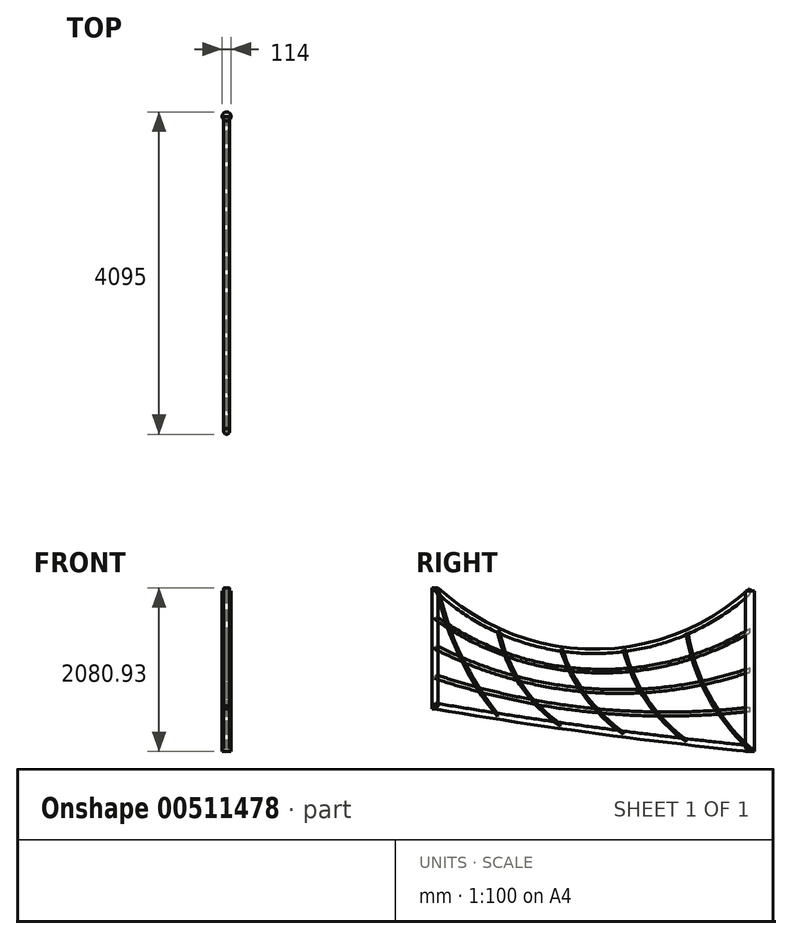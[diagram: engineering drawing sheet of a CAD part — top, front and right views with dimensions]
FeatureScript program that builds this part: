
annotation { "Feature Type Name" : "Feature", "Feature Type Description" : "" }
export const myFeature = defineFeature(function(context is Context, id is Id, definition is map)
    precondition{}
    {
        {
            var Q0;
            Q0=qCreatedBy(makeId("Right.planeOp"),FACE);
            var sketch = newSketch(context, id + "F0", { "sketchPlane" : qUnion([Q0])});
            skLineSegment(sketch, "E0.top", {"start": v(0, 2000) * mm, "end": v(-4000, 2000) * mm});
            skLineSegment(sketch, "E0.left", {"start": v(0, 0) * mm, "end": v(0, 2000) * mm});
            skLineSegment(sketch, "E0.right", {"start": v(-4000, 0) * mm, "end": v(-4000, 2000) * mm});
            skPoint(sketch, "E1", {"position": v(-4000, 540) * mm});
            skPoint(sketch, "E2", {"position": v(-4000, 915) * mm});
            skPoint(sketch, "E3", {"position": v(-4000, 1290) * mm});
            skPoint(sketch, "E4", {"position": v(-4000, 2040) * mm});
            skPoint(sketch, "E5", {"position": v(0, 500) * mm});
            skPoint(sketch, "E6", {"position": v(0, 1000) * mm});
            skPoint(sketch, "E7", {"position": v(0, 1500) * mm});
            skPoint(sketch, "E8", {"position": v(-4000, 1665) * mm});
            skPoint(sketch, "E9", {"position": v(-2000, 0) * mm});
            skPoint(sketch, "E10", {"position": v(-2000, 486.4) * mm});
            skPoint(sketch, "E11", {"position": v(-2000, 736.4) * mm});
            skPoint(sketch, "E12", {"position": v(-2000, 1236.4) * mm});
            skPoint(sketch, "E13", {"position": v(-2000, 986.4) * mm});
            skArc(sketch, "E14", {"start": v(-4000, 540) * mm, "mid": v(-2004.45, 237) * mm, "end": v(0, 0) * mm});
            skPoint(sketch, "E15", {"position": v(-2000, 236.4) * mm});
            skArc(sketch, "E16", {"start": v(-4000, 915) * mm, "mid": v(-2022.7, 488.74) * mm, "end": v(0, 500) * mm});
            skArc(sketch, "E17", {"start": v(-4000, 1290) * mm, "mid": v(-2029.47, 738.46) * mm, "end": v(0, 1000) * mm});
            skArc(sketch, "E18", {"start": v(-4000, 1665) * mm, "mid": v(-2024.55, 987.34) * mm, "end": v(0, 1500) * mm});
            skArc(sketch, "E19", {"start": v(-4000, 2040) * mm, "mid": v(-2007.84, 1236.48) * mm, "end": v(0, 2000) * mm});
            skSolve(sketch);
        }
        {
            var Q0;
            Q0=qCreatedBy(makeId("Front.planeOp"),FACE);
            var sketch = newSketch(context, id + "F1", { "sketchPlane" : qUnion([Q0])});
            skCircle(sketch, "E20", {"center": v(0, 0) * mm, "radius": 38 * mm});
            skCircle(sketch, "E21", {"center": v(0, 500) * mm, "radius": 25.5 * mm});
            skCircle(sketch, "E22", {"center": v(0, 1000) * mm, "radius": 25.5 * mm});
            skCircle(sketch, "E23", {"center": v(0, 1500) * mm, "radius": 25.5 * mm});
            skCircle(sketch, "E24", {"center": v(0, 2000) * mm, "radius": 38 * mm});
            skSolve(sketch);
        }
        {
            var Q0;
            Q0=makeQuery(id+"F1.imprint","IMPRINT",FACE,{"disambiguationData":[TD([[makeQuery(id+"F1.imprint","IMPRINT",EDGE,{"derivedFrom":sQuery(id+"F1.wireOp",EDGE,"E20")}),1.0]])]});
            var Q1;
            Q1=sQuery(id+"F0.wireOp",EDGE,"E14");
            sweep(context, id + "F2", {"profiles" : qUnion([Q0]), "path" : qUnion([Q1])});
        }
        {
            var Q0;
            Q0=makeQuery(id+"F1.imprint","IMPRINT",FACE,{"disambiguationData":[TD([[makeQuery(id+"F1.imprint","IMPRINT",EDGE,{"derivedFrom":sQuery(id+"F1.wireOp",EDGE,"E21")}),1.0]])]});
            var Q1;
            Q1=sQuery(id+"F0.wireOp",EDGE,"E16");
            sweep(context, id + "F3", {"profiles" : qUnion([Q0]), "path" : qUnion([Q1])});
        }
        {
            var Q0;
            Q0=makeQuery(id+"F1.imprint","IMPRINT",FACE,{"disambiguationData":[TD([[makeQuery(id+"F1.imprint","IMPRINT",EDGE,{"derivedFrom":sQuery(id+"F1.wireOp",EDGE,"E22")}),1.0]])]});
            var Q1;
            Q1=sQuery(id+"F0.wireOp",EDGE,"E17");
            sweep(context, id + "F4", {"profiles" : qUnion([Q0]), "path" : qUnion([Q1])});
        }
        {
            var Q0;
            Q0=makeQuery(id+"F1.imprint","IMPRINT",FACE,{"disambiguationData":[TD([[makeQuery(id+"F1.imprint","IMPRINT",EDGE,{"derivedFrom":sQuery(id+"F1.wireOp",EDGE,"E23")}),1.0]])]});
            var Q1;
            Q1=sQuery(id+"F0.wireOp",EDGE,"E18");
            sweep(context, id + "F5", {"profiles" : qUnion([Q0]), "path" : qUnion([Q1])});
        }
        {
            var Q0;
            Q0=makeQuery(id+"F1.imprint","IMPRINT",FACE,{"disambiguationData":[TD([[makeQuery(id+"F1.imprint","IMPRINT",EDGE,{"derivedFrom":sQuery(id+"F1.wireOp",EDGE,"E24")}),1.0]])]});
            var Q1;
            Q1=sQuery(id+"F0.wireOp",EDGE,"E19");
            sweep(context, id + "F6", {"profiles" : qUnion([Q0]), "path" : qUnion([Q1])});
        }
        {
            var Q0;
            Q0=qCreatedBy(makeId("Top.planeOp"),FACE);
            var sketch = newSketch(context, id + "F7", { "sketchPlane" : qUnion([Q0])});
            skCircle(sketch, "E25", {"center": v(0, 0) * mm, "radius": 57 * mm});
            skSolve(sketch);
        }
        {
            var Q0;
            Q0=makeQuery(id+"F7.imprint","IMPRINT",FACE,{"disambiguationData":[TD([[makeQuery(id+"F7.imprint","IMPRINT",EDGE,{"derivedFrom":sQuery(id+"F7.wireOp",EDGE,"E25")}),1.0]])]});
            extrude(context, id + "F8", {"entities" : qUnion([Q0]), "depth" : 2000 * mm});
        }
        {
            var Q0;
            Q0=qCreatedBy(makeId("Top.planeOp"),FACE);
            cPlane(context, id + "F9", {"entities" : qUnion([Q0]), "cplaneType" : CPlaneType.OFFSET, "offset" : 540 * mm, "width" : 150 * mm, "height" : 150 * mm});
        }
        {
            var Q0;
            Q0=qCreatedBy(id+"F9.planeOp",FACE);
            var sketch = newSketch(context, id + "F10", { "sketchPlane" : qUnion([Q0])});
            skPoint(sketch, "E26", {"position": v(0, 0) * mm});
            skCircle(sketch, "E27", {"center": v(0, -4000) * mm, "radius": 38 * mm});
            skSolve(sketch);
        }
        {
            var Q0;
            Q0=makeQuery(id+"F10.imprint","IMPRINT",FACE,{"disambiguationData":[TD([[makeQuery(id+"F10.imprint","IMPRINT",EDGE,{"derivedFrom":sQuery(id+"F10.wireOp",EDGE,"E27")}),1.0]])]});
            extrude(context, id + "F11", {"entities" : qUnion([Q0]), "depth" : 1500 * mm});
        }
        {
            var Q0;
            Q0=makeQuery(id+"F11.opExtrude","CAP_FACE",FACE,{"disambiguationData":[OSD([sQuery(id+"F10.wireOp",EDGE,"E27")])],"isStart":true});
            extrude(context, id + "F12", {"entities" : qUnion([Q0]), "depth" : 38 * mm});
        }
        {
            var Q0;
            Q0=makeQuery(id+"F8.opExtrude","CAP_FACE",FACE,{"disambiguationData":[OSD([sQuery(id+"F7.wireOp",EDGE,"E25")])],"isStart":true});
            extrude(context, id + "F13", {"entities" : qUnion([Q0]), "depth" : 38 * mm});
        }
        {
            var Q0;
            Q0=qCreatedBy(makeId("Right.planeOp"),FACE);
            var sketch = newSketch(context, id + "F14", { "sketchPlane" : qUnion([Q0])});
            skLineSegment(sketch, "E28.bottom", {"start": v(0, 0) * mm, "end": v(-4000, 0) * mm});
            skLineSegment(sketch, "E28.top", {"start": v(0, 2000) * mm, "end": v(-4000, 2000) * mm});
            skLineSegment(sketch, "E28.left", {"start": v(0, 0) * mm, "end": v(0, 2000) * mm});
            skLineSegment(sketch, "E28.right", {"start": v(-4000, 0) * mm, "end": v(-4000, 2000) * mm});
            skPoint(sketch, "E29", {"position": v(-800, 0) * mm});
            skPoint(sketch, "E30", {"position": v(-1600, 0) * mm});
            skPoint(sketch, "E31", {"position": v(-2400, 0) * mm});
            skPoint(sketch, "E32", {"position": v(-3200, 0) * mm});
            skArc(sketch, "E33", {"start": v(-800, 1473.46) * mm, "mid": v(-526.2, 668.22) * mm, "end": v(0, 0) * mm});
            skArc(sketch, "E34", {"start": v(-1600, 1261.87) * mm, "mid": v(-1305.15, 605.62) * mm, "end": v(-800, 93.33) * mm});
            skArc(sketch, "E35", {"start": v(-2400, 1271.5) * mm, "mid": v(-2088.51, 665.06) * mm, "end": v(-1600, 189.5) * mm});
            skArc(sketch, "E36", {"start": v(-3200, 1502.32) * mm, "mid": v(-2915.16, 820.38) * mm, "end": v(-2400, 290.5) * mm});
            skArc(sketch, "E37", {"start": v(-3961.24, 2000) * mm, "mid": v(-3673.83, 1162.98) * mm, "end": v(-3200, 415.52) * mm});
            skArc(sketch, "E38.0", {"start": v(-812.54, 1471.46) * mm, "mid": v(-537.35, 662.16) * mm, "end": v(-8.5, -9.43) * mm});
            skArc(sketch, "E39.0", {"start": v(-787.46, 1475.46) * mm, "mid": v(-515.03, 674.28) * mm, "end": v(8.5, 9.43) * mm});
            skArc(sketch, "E40.0", {"start": v(-1612.32, 1258.8) * mm, "mid": v(-1315.63, 598.44) * mm, "end": v(-807.32, 82.95) * mm});
            skArc(sketch, "E41.0", {"start": v(-1587.68, 1264.95) * mm, "mid": v(-1294.67, 612.8) * mm, "end": v(-792.68, 103.7) * mm});
            skArc(sketch, "E42.0", {"start": v(-2412.09, 1267.6) * mm, "mid": v(-2098.72, 657.5) * mm, "end": v(-1607.27, 179.1) * mm});
            skArc(sketch, "E43.0", {"start": v(-2387.91, 1275.4) * mm, "mid": v(-2078.3, 672.6) * mm, "end": v(-1592.73, 199.92) * mm});
            skArc(sketch, "E44.0", {"start": v(-3212.43, 1499.7) * mm, "mid": v(-2925.76, 813.38) * mm, "end": v(-2407.3, 280.1) * mm});
            skArc(sketch, "E45.0", {"start": v(-3187.57, 1504.94) * mm, "mid": v(-2904.56, 827.38) * mm, "end": v(-2392.7, 300.9) * mm});
            skArc(sketch, "E46.0", {"start": v(-3973.65, 1997.3) * mm, "mid": v(-3685.28, 1157.48) * mm, "end": v(-3209.86, 407.52) * mm});
            skArc(sketch, "E47.0", {"start": v(-3948.83, 2002.7) * mm, "mid": v(-3662.39, 1168.48) * mm, "end": v(-3190.14, 423.53) * mm});
            skLineSegment(sketch, "E48", {"start": v(-3973.65, 1997.3) * mm, "end": v(-3948.83, 2002.7) * mm});
            skLineSegment(sketch, "E49", {"start": v(-3212.43, 1499.7) * mm, "end": v(-3187.57, 1504.94) * mm});
            skLineSegment(sketch, "E50", {"start": v(-2412.09, 1267.6) * mm, "end": v(-2387.91, 1275.4) * mm});
            skLineSegment(sketch, "E51", {"start": v(-1587.68, 1264.95) * mm, "end": v(-1612.32, 1258.8) * mm});
            skLineSegment(sketch, "E52", {"start": v(-787.46, 1475.46) * mm, "end": v(-812.54, 1471.46) * mm});
            skLineSegment(sketch, "E53", {"start": v(-8.5, -9.43) * mm, "end": v(8.5, 9.43) * mm});
            skLineSegment(sketch, "E54", {"start": v(-807.32, 82.95) * mm, "end": v(-792.68, 103.7) * mm});
            skLineSegment(sketch, "E55", {"start": v(-1607.27, 179.1) * mm, "end": v(-1592.73, 199.92) * mm});
            skLineSegment(sketch, "E56", {"start": v(-2407.3, 280.1) * mm, "end": v(-2392.7, 300.9) * mm});
            skLineSegment(sketch, "E57", {"start": v(-3209.86, 407.52) * mm, "end": v(-3190.14, 423.53) * mm});
            skSolve(sketch);
        }
        {
            var Q0;
            {var subQ0=sQuery(id+"F14.wireOp",EDGE,"E33");Q0=makeQuery(id+"F14.imprint","IMPRINT",FACE,{"disambiguationData":[TD([[makeQuery(id+"F14.imprint","IMPRINT",EDGE,{"derivedFrom":subQ0}),-1.0]])]});}
            var Q1;
            {var subQ0=sQuery(id+"F14.wireOp",EDGE,"E33");Q1=makeQuery(id+"F14.imprint","IMPRINT",FACE,{"disambiguationData":[TD([[makeQuery(id+"F14.imprint","IMPRINT",EDGE,{"derivedFrom":subQ0}),1.0]])]});}
            var Q2;
            {var subQ0=sQuery(id+"F14.wireOp",EDGE,"E34");Q2=makeQuery(id+"F14.imprint","IMPRINT",FACE,{"disambiguationData":[TD([[makeQuery(id+"F14.imprint","IMPRINT",EDGE,{"derivedFrom":subQ0}),1.0]])]});}
            var Q3;
            {var subQ0=sQuery(id+"F14.wireOp",EDGE,"E34");Q3=makeQuery(id+"F14.imprint","IMPRINT",FACE,{"disambiguationData":[TD([[makeQuery(id+"F14.imprint","IMPRINT",EDGE,{"derivedFrom":subQ0}),-1.0]])]});}
            var Q4;
            {var subQ0=sQuery(id+"F14.wireOp",EDGE,"E35");Q4=makeQuery(id+"F14.imprint","IMPRINT",FACE,{"disambiguationData":[TD([[makeQuery(id+"F14.imprint","IMPRINT",EDGE,{"derivedFrom":subQ0}),1.0]])]});}
            var Q5;
            {var subQ0=sQuery(id+"F14.wireOp",EDGE,"E35");Q5=makeQuery(id+"F14.imprint","IMPRINT",FACE,{"disambiguationData":[TD([[makeQuery(id+"F14.imprint","IMPRINT",EDGE,{"derivedFrom":subQ0}),-1.0]])]});}
            var Q6;
            {var subQ0=sQuery(id+"F14.wireOp",EDGE,"E36");Q6=makeQuery(id+"F14.imprint","IMPRINT",FACE,{"disambiguationData":[TD([[makeQuery(id+"F14.imprint","IMPRINT",EDGE,{"derivedFrom":subQ0}),1.0]])]});}
            var Q7;
            {var subQ0=sQuery(id+"F14.wireOp",EDGE,"E36");Q7=makeQuery(id+"F14.imprint","IMPRINT",FACE,{"disambiguationData":[TD([[makeQuery(id+"F14.imprint","IMPRINT",EDGE,{"derivedFrom":subQ0}),-1.0]])]});}
            var Q8;
            {var subQ0=sQuery(id+"F14.wireOp",EDGE,"E37");Q8=makeQuery(id+"F14.imprint","IMPRINT",FACE,{"disambiguationData":[TD([[makeQuery(id+"F14.imprint","IMPRINT",EDGE,{"derivedFrom":subQ0}),-1.0]])]});}
            var Q9;
            {var subQ0=sQuery(id+"F14.wireOp",EDGE,"E37");Q9=makeQuery(id+"F14.imprint","IMPRINT",FACE,{"disambiguationData":[TD([[makeQuery(id+"F14.imprint","IMPRINT",EDGE,{"derivedFrom":subQ0}),1.0]])]});}
            extrude(context, id + "F15", {"entities" : qUnion([Q0, Q1, Q2, Q3, Q4, Q5, Q6, Q7, Q8, Q9]), "endBound" : BoundingType.SYMMETRIC, "depth" : 25.4 * mm});
        }
    });
